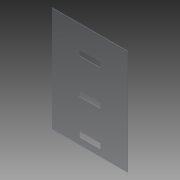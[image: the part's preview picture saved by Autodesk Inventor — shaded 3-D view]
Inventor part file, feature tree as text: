
AUTODESK INVENTOR PART (.ipt)
format: ipt  version: 2013 (Build 170138000, 138)  size: 119,296 bytes
history: native  units: in
note: dims shown in document units (in); Inventor stores cm internally (conversion verified against a paired STEP export)
features: sketch x3, extrude x2, hole x1
ambient origin geometry x8: Origin, YZ Plane, XZ Plane, XY Plane, X Axis, Y Axis, Z Axis, Center Point
bodies: Solid1 (feature_tree)
feature tree (6):
  extrude  "Extrusion1"  Depth=59.75in
  extrude  "Extrusion2"  Depth=13.0in
  hole  "Hole1"  [1 undecoded]
  sketch  "Sketch1"  dims[d0=43.0in d1=59.75in]
  sketch  "Sketch2"  dims[d2=0.25in d3=0.0in d4=13.0in]
  sketch  "Sketch3"  dims[d5=16.0in d6=33.0in d7=36.0in d8=53.0in d9=56.0in d10=15.5in d11=27.5in d12=0.25in d13=0.0in d14=1.5in d16=40.0in d17=9.0in d18=10.49in d20=30.0in d21=31.49in d22=58.75in d23=3.0in d24=40.0in d25=0.38in d26=0.75in d27=0.375in d28=0.25in d29=0.5635in d30=1.0in d31=0.8108in d32=21.5in]
note: 1 required parameter value undecoded (feature->parameter linkage not recoverable at this tier; creation-order binding heuristic only, values carry confidence <= 0.55)
